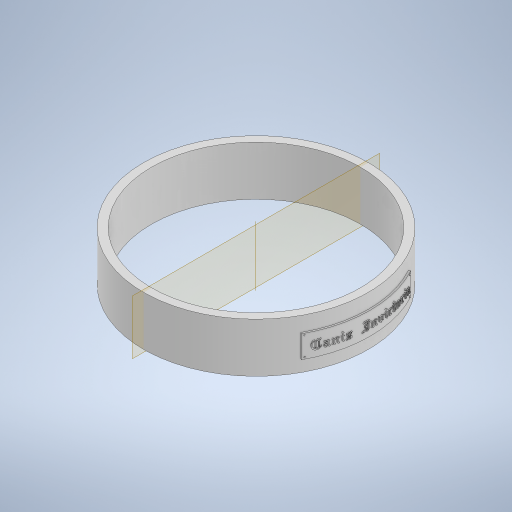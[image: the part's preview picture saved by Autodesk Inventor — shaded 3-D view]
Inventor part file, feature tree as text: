
AUTODESK INVENTOR PART (.ipt)
format: ipt  version: 2023 (Build 270158000, 158)  size: 5,790,208 bytes
history: native  units: in
note: dims shown in document units (in); Inventor stores cm internally (conversion verified against a paired STEP export)
features: emboss x3, pattern_circular x3, other x2, extrude x1, plane x1, fillet x1, sketch x1
ambient origin geometry x8: Origin, YZ Plane, XZ Plane, XY Plane, X Axis, Y Axis, Z Axis, Center Point
bodies: Solid1 (feature_tree)
feature tree (12):
  extrude  "Extrusion1"  Depth=1.9685in
  plane  "Work Plane1"
  other  "Text"
  emboss  "Emboss4"
  emboss  "Emboss5"
  emboss  "Emboss6"
  fillet  "Rivots"  Radius=0.8661in
  pattern_circular  "Circular Pattern1"  Count=6  [1 undecoded]
  pattern_circular  "Circular Pattern2"  [2 undecoded]
  pattern_circular  "Circular Pattern3"  [2 undecoded]
  sketch  "Sketch1"  dims[d0=3.937in d1=3.6614in d2=0.8661in d3=0.0in d4=2.3622in d6=0.4546in d10=0.0in d11=0.3937in d12=1.9685in d19=0.0in d20=0.0in d21=0.0295in d22=0.0in d23=0.0197in d24=0.0in d25=0.0295in d26=0.0295in d27=0.0295in d28=0.0157in d29=0.0in d30=0.0138in d31=0.7874in d32=360.0deg d34=0.7874in d35=360.0deg d37=0.7874in d38=360.0deg d33=0.0in]
  other  "NamePlate"
note: 5 required parameter values undecoded (feature->parameter linkage not recoverable at this tier; creation-order binding heuristic only, values carry confidence <= 0.55)
